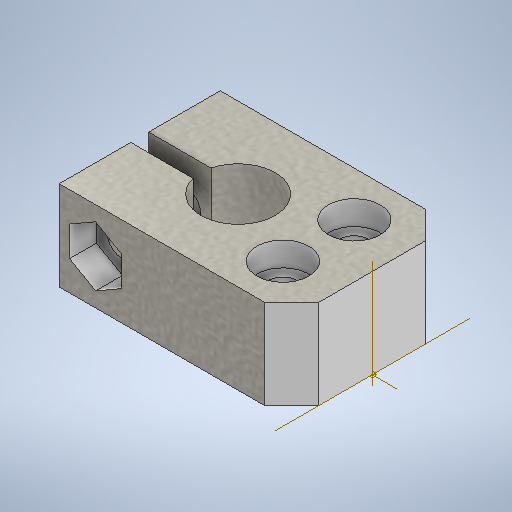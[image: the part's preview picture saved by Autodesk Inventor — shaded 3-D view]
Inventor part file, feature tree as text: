
AUTODESK INVENTOR PART (.ipt)
format: ipt  version: 2025.2 (Build 292293000, 293)  size: 367,616 bytes
history: native  units: mm
features: sketch x5, extrude x4, hole x1, chamfer x1
ambient origin geometry x8: Origin, YZ Plane, XZ Plane, XY Plane, X Axis, Y Axis, Z Axis, Center Point
bodies: Solid1 (feature_tree)
feature tree (11):
  extrude  "Extrusion1"  Depth=9.0mm
  hole  "Hole1"  [1 undecoded]
  extrude  "Extrusion3"  Depth=3.5mm
  extrude  "Extrusion4"  Depth=5.8mm
  extrude  "Extrusion5"  Depth=5.8mm
  chamfer  "Chamfer1"  Distance=2.0mm
  sketch  "Sketch1"  dims[d2=1.0mm d3=9.0mm]
  sketch  "Sketch3"  dims[d4=8.3mm d8=10.0mm d9=0.0mm]
  sketch  "Sketch4"  dims[d15=3.5mm d17=3.5mm]
  sketch  "Sketch5"  dims[d18=0.0mm d20=5.8mm]
  sketch  "Sketch7"  dims[d21=3.0mm d22=0.0mm d23=5.8mm d24=2.0mm d25=0.0mm d27=15.0mm d28=26.0mm d34=3.3mm d35=6.0mm d36=5.8mm d37=2.7mm d38=90.0deg d39=8.0mm d40=20.594885mm d41=3.0mm d42=2.0mm d43=45.0deg d44=8.0mm d45=9.0mm d46=7.0mm]
note: 1 required parameter value undecoded (feature->parameter linkage not recoverable at this tier; creation-order binding heuristic only, values carry confidence <= 0.55)
